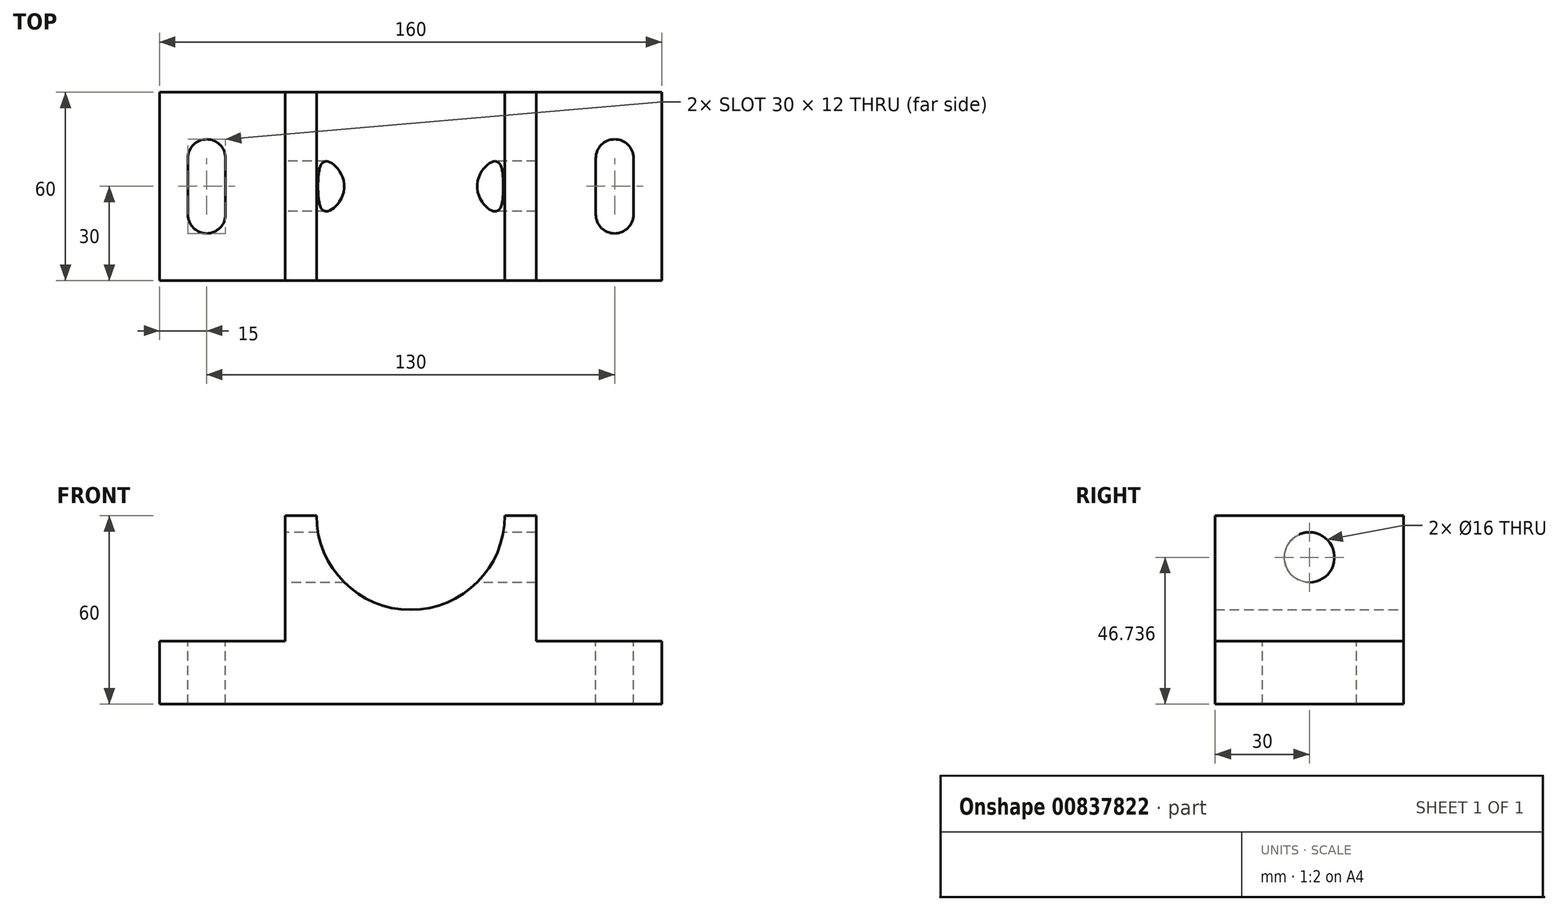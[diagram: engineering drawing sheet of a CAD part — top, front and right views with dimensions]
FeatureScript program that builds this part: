
annotation { "Feature Type Name" : "Feature", "Feature Type Description" : "" }
export const myFeature = defineFeature(function(context is Context, id is Id, definition is map)
    precondition{}
    {
        {
            var Q0;
            Q0=qCreatedBy(makeId("Front.planeOp"),FACE);
            var sketch = newSketch(context, id + "F0", { "sketchPlane" : qUnion([Q0])});
            skLineSegment(sketch, "E0.bottom", {"start": v(-80, -10) * mm, "end": v(80, -10) * mm});
            skLineSegment(sketch, "E0.top", {"start": v(-80, 10) * mm, "end": v(-40, 10) * mm});
            skLineSegment(sketch, "E0.left", {"start": v(-80, -10) * mm, "end": v(-80, 10) * mm});
            skLineSegment(sketch, "E0.right", {"start": v(80, -10) * mm, "end": v(80, 10) * mm});
            skPoint(sketch, "E0.middle", {"position": v(0, 0) * mm});
            skLineSegment(sketch, "E1.bottom", {"start": v(-40, 50) * mm, "end": v(-30, 50) * mm});
            skLineSegment(sketch, "E1.left", {"start": v(-40, 50) * mm, "end": v(-40, 10) * mm});
            skLineSegment(sketch, "E1.right", {"start": v(40, 50) * mm, "end": v(40, 10) * mm});
            skPoint(sketch, "E1.middle", {"position": v(0, 10) * mm});
            skPoint(sketch, "E2.orphan", {"position": v(40, -30) * mm});
            skPoint(sketch, "E3.trimOffspring.end.orphan", {"position": v(-40, -30) * mm});
            skLineSegment(sketch, "E4", {"start": v(40, 50) * mm, "end": v(40, 30) * mm});
            skArc(sketch, "E5", {"start": v(-30, 50) * mm, "mid": v(0, 20) * mm, "end": v(30, 50) * mm});
            skLineSegment(sketch, "E6.trimOffspring", {"start": v(30, 50) * mm, "end": v(40, 50) * mm});
            skLineSegment(sketch, "E7.trimOffspring", {"start": v(40, 10) * mm, "end": v(80, 10) * mm});
            skSolve(sketch);
        }
        {
            var Q0;
            Q0 = qSketchRegion(id + "F0", true);
            extrude(context, id + "F1", {"entities" : qUnion([Q0]), "depth" : 60 * mm, "offsetDistance" : 25 * mm});
        }
        {
            var Q0;
            Q0=makeQuery(id+"F1.opExtrude","SWEPT_FACE",FACE,{"disambiguationData":[OSD([sQuery(id+"F0.wireOp",EDGE,"E1.left")])]});
            var sketch = newSketch(context, id + "F2", { "sketchPlane" : qUnion([Q0])});
            skLineSegment(sketch, "E8", {"start": v(0, -8.26) * mm, "end": v(0, 36.74) * mm});
            skCircle(sketch, "E9", {"center": v(30, 36.74) * mm, "radius": 8 * mm});
            skPoint(sketch, "E9.centerSnap0", {"position": v(30, 10) * mm});
            skPoint(sketch, "E9.perimeterSnap0", {"position": v(30, 10) * mm});
            skPoint(sketch, "E9.perimeterSnap1", {"position": v(0, 30) * mm});
            skSolve(sketch);
        }
        {
            var Q0;
            Q0=makeQuery(id+"F2.imprint","IMPRINT",FACE,{"disambiguationData":[TD([[makeQuery(id+"F2.imprint","IMPRINT",EDGE,{"derivedFrom":sQuery(id+"F2.wireOp",EDGE,"E9")}),1.0]])]});
            extrude(context, id + "F3", {"entities" : qUnion([Q0]), "operationType" : NewBodyOperationType.REMOVE, "endBound" : BoundingType.THROUGH_ALL, "oppositeDirection" : true, "depth" : 25 * mm, "offsetDistance" : 25 * mm});
        }
        {
            var Q0;
            Q0=makeQuery(id+"F1.opExtrude","SWEPT_FACE",FACE,{"disambiguationData":[OSD([sQuery(id+"F0.wireOp",EDGE,"E0.top")])]});
            var sketch = newSketch(context, id + "F4", { "sketchPlane" : qUnion([Q0])});
            skPoint(sketch, "E10.middle.positionSnap0", {"position": v(-60, 0) * mm});
            skPoint(sketch, "E10.middle.positionSnap1", {"position": v(-80, -30) * mm});
            skPoint(sketch, "E10.centerSnap0", {"position": v(-60, 0) * mm});
            skPoint(sketch, "E10.centerSnap1", {"position": v(-80, -30) * mm});
            skLineSegment(sketch, "E11", {"start": v(-80, -60) * mm, "end": v(-65, -60) * mm});
            skLineSegment(sketch, "E12.bottom", {"start": v(-65, -45) * mm, "end": v(-65, -45) * mm});
            skLineSegment(sketch, "E12.top", {"start": v(-65, -15) * mm, "end": v(-65, -15) * mm});
            skLineSegment(sketch, "E12.left", {"start": v(-71, -39) * mm, "end": v(-71, -21) * mm});
            skLineSegment(sketch, "E12.right", {"start": v(-59, -39) * mm, "end": v(-59, -21) * mm});
            skPoint(sketch, "E12.middle", {"position": v(-65, -30) * mm});
            skPoint(sketch, "E13.visualSharp", {"position": v(-71, -15) * mm});
            skArc(sketch, "E13.filletArc", {"start": v(-65, -15) * mm, "mid": v(-69.24, -16.76) * mm, "end": v(-71, -21) * mm});
            skPoint(sketch, "E14.visualSharp", {"position": v(-59, -15) * mm});
            skArc(sketch, "E14.filletArc", {"start": v(-59, -21) * mm, "mid": v(-60.76, -16.76) * mm, "end": v(-65, -15) * mm});
            skPoint(sketch, "E15.visualSharp", {"position": v(-59, -45) * mm});
            skArc(sketch, "E15.filletArc", {"start": v(-65, -45) * mm, "mid": v(-60.76, -43.24) * mm, "end": v(-59, -39) * mm});
            skPoint(sketch, "E16.visualSharp", {"position": v(-71, -45) * mm});
            skArc(sketch, "E16.filletArc", {"start": v(-71, -39) * mm, "mid": v(-69.24, -43.24) * mm, "end": v(-65, -45) * mm});
            skSolve(sketch);
        }
        {
            var Q0;
            Q0=makeQuery(id+"F1.opExtrude","SWEPT_FACE",FACE,{"disambiguationData":[OSD([sQuery(id+"F0.wireOp",EDGE,"E7.trimOffspring")])]});
            var sketch = newSketch(context, id + "F5", { "sketchPlane" : qUnion([Q0])});
            skLineSegment(sketch, "E17", {"start": v(80, -60) * mm, "end": v(65, -60) * mm});
            skPoint(sketch, "E18.middle.positionSnap0", {"position": v(80, -30) * mm});
            skPoint(sketch, "E18.centerSnap0", {"position": v(80, -30) * mm});
            skLineSegment(sketch, "E19.bottom", {"start": v(65, -45) * mm, "end": v(65, -45) * mm});
            skLineSegment(sketch, "E19.top", {"start": v(65, -15) * mm, "end": v(65, -15) * mm});
            skLineSegment(sketch, "E19.left", {"start": v(59, -39) * mm, "end": v(59, -21) * mm});
            skLineSegment(sketch, "E19.right", {"start": v(71, -39) * mm, "end": v(71, -21) * mm});
            skPoint(sketch, "E19.middle", {"position": v(65, -30) * mm});
            skPoint(sketch, "E20.visualSharp", {"position": v(59, -15) * mm});
            skArc(sketch, "E20.filletArc", {"start": v(65, -15) * mm, "mid": v(60.76, -16.76) * mm, "end": v(59, -21) * mm});
            skPoint(sketch, "E21.visualSharp", {"position": v(71, -15) * mm});
            skArc(sketch, "E21.filletArc", {"start": v(71, -21) * mm, "mid": v(69.24, -16.76) * mm, "end": v(65, -15) * mm});
            skPoint(sketch, "E22.visualSharp", {"position": v(71, -45) * mm});
            skArc(sketch, "E22.filletArc", {"start": v(65, -45) * mm, "mid": v(69.24, -43.24) * mm, "end": v(71, -39) * mm});
            skPoint(sketch, "E23.visualSharp", {"position": v(59, -45) * mm});
            skArc(sketch, "E23.filletArc", {"start": v(59, -39) * mm, "mid": v(60.76, -43.24) * mm, "end": v(65, -45) * mm});
            skSolve(sketch);
        }
        {
            var Q0;
            Q0=makeQuery(id+"F4.imprint","IMPRINT",FACE,{"disambiguationData":[TD([[makeQuery(id+"F4.imprint","IMPRINT",EDGE,{"derivedFrom":sQuery(id+"F4.wireOp",EDGE,"E12.left")}),-1.0]])]});
            var Q1;
            Q1=makeQuery(id+"F5.imprint","IMPRINT",FACE,{"disambiguationData":[TD([[makeQuery(id+"F5.imprint","IMPRINT",EDGE,{"derivedFrom":sQuery(id+"F5.wireOp",EDGE,"E19.left")}),-1.0]])]});
            extrude(context, id + "F6", {"entities" : qUnion([Q0, Q1]), "operationType" : NewBodyOperationType.REMOVE, "endBound" : BoundingType.THROUGH_ALL, "oppositeDirection" : true, "depth" : 25 * mm, "offsetDistance" : 25 * mm});
        }
    });
